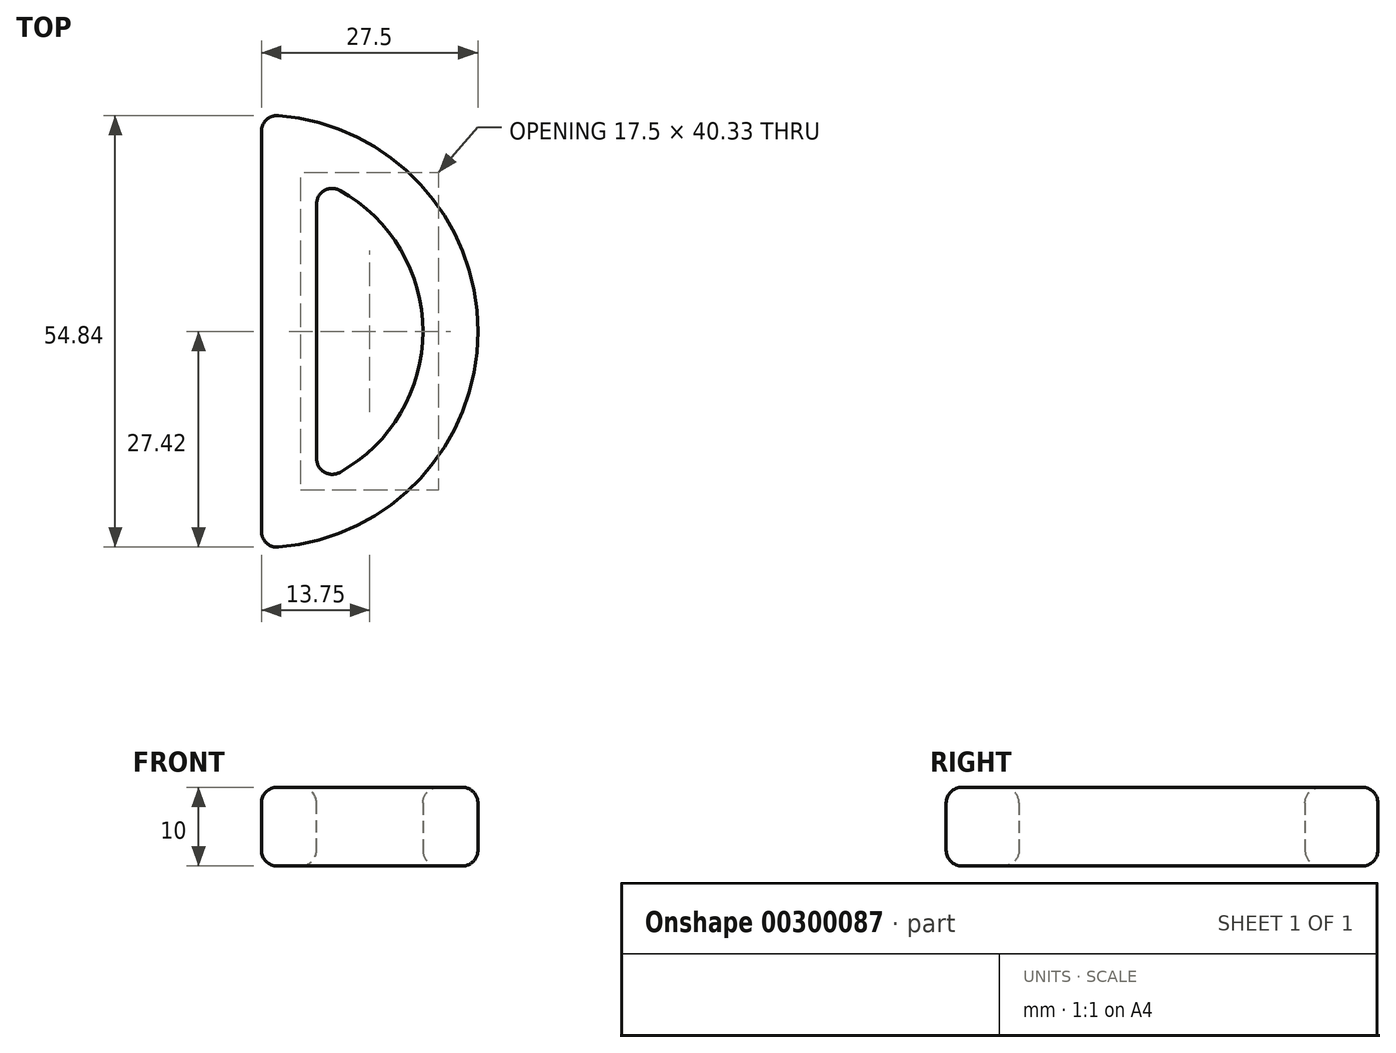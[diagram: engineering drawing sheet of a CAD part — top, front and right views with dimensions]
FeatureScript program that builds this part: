
annotation { "Feature Type Name" : "Feature", "Feature Type Description" : "" }
export const myFeature = defineFeature(function(context is Context, id is Id, definition is map)
    precondition{}
    {
        {
            var Q0;
            Q0=qCreatedBy(makeId("Top.planeOp"),FACE);
            var sketch = newSketch(context, id + "F0", { "sketchPlane" : qUnion([Q0])});
            skLineSegment(sketch, "E0", {"start": v(0, 0) * mm, "end": v(0, 55) * mm});
            skArc(sketch, "E1", {"start": v(0, 55) * mm, "mid": v(27.5, 27.5) * mm, "end": v(0, 0) * mm});
            skArc(sketch, "E2.0", {"start": v(0, 48) * mm, "mid": v(20.5, 27.5) * mm, "end": v(0, 7) * mm});
            skLineSegment(sketch, "E3", {"start": v(0, 27.5) * mm, "end": v(7, 27.5) * mm});
            skLineSegment(sketch, "E4", {"start": v(7, 27.5) * mm, "end": v(7, 46.77) * mm});
            skLineSegment(sketch, "E5", {"start": v(7, 27.5) * mm, "end": v(7, 8.23) * mm});
            skSolve(sketch);
        }
        {
            var Q0;
            Q0 = qSketchRegion(id + "F0", true);
            extrude(context, id + "F1", {"entities" : qUnion([Q0]), "depth" : 10 * mm});
        }
        {
            var Q0;
            Q0=makeQuery(id+"F1.opExtrude","SWEPT_FACE",FACE,{"disambiguationData":[OSD([sQuery(id+"F0.wireOp",EDGE,"E1")])]});
            var Q1;
            Q1=makeQuery(id+"F1.opExtrude","CAP_EDGE",EDGE,{"disambiguationData":[OSD([sQuery(id+"F0.wireOp",EDGE,"E2.0")])],"isStart":false});
            var Q2;
            Q2=makeQuery(id+"F1.opExtrude","CAP_EDGE",EDGE,{"disambiguationData":[OSD([sQuery(id+"F0.wireOp",EDGE,"E4"),sQuery(id+"F0.wireOp",EDGE,"E5")])],"isStart":false});
            var Q3;
            Q3=makeQuery(id+"F1.opExtrude","CAP_EDGE",EDGE,{"disambiguationData":[OSD([sQuery(id+"F0.wireOp",EDGE,"E0")])],"isStart":false});
            var Q4;
            Q4=makeQuery(id+"F1.opExtrude","CAP_EDGE",EDGE,{"disambiguationData":[OSD([sQuery(id+"F0.wireOp",EDGE,"E1")])],"isStart":false});
            var Q5;
            {var subQ0=sQuery(id+"F0.wireOp",EDGE,"E1");var subQ1=sQuery(id+"F0.wireOp",EDGE,"E0");Q5=makeQuery(id+"F1.opExtrude","SWEPT_EDGE",EDGE,{"disambiguationData":[OSD([subQ1,subQ0]),TDD([makeQuery(id+"F0.imprint","INTERSECT",VERTEX,{"disambiguationData":[OD(0.0)],"derivedFrom":[subQ1,subQ0]})])]});}
            var Q6;
            Q6=makeQuery(id+"F1.opExtrude","CAP_EDGE",EDGE,{"disambiguationData":[OSD([sQuery(id+"F0.wireOp",EDGE,"E2.0")])],"isStart":true});
            var Q7;
            Q7=makeQuery(id+"F1.opExtrude","CAP_EDGE",EDGE,{"disambiguationData":[OSD([sQuery(id+"F0.wireOp",EDGE,"E0")])],"isStart":true});
            var Q8;
            Q8=makeQuery(id+"F1.opExtrude","CAP_EDGE",EDGE,{"disambiguationData":[OSD([sQuery(id+"F0.wireOp",EDGE,"E4"),sQuery(id+"F0.wireOp",EDGE,"E5")])],"isStart":true});
            var Q9;
            Q9=makeQuery(id+"F1.opExtrude","SWEPT_EDGE",EDGE,{"disambiguationData":[OSD([sQuery(id+"F0.wireOp",EDGE,"E2.0"),sQuery(id+"F0.wireOp",EDGE,"E5")])]});
            var Q10;
            Q10=makeQuery(id+"F1.opExtrude","SWEPT_FACE",FACE,{"disambiguationData":[OSD([sQuery(id+"F0.wireOp",EDGE,"E4"),sQuery(id+"F0.wireOp",EDGE,"E5")])]});
            fillet(context, id + "F2", {"entities" : qUnion([Q0, Q1, Q2, Q3, Q4, Q5, Q6, Q7, Q8, Q9, Q10]), "radius" : 2 * mm, "tangentPropagation" : true, "allowEdgeOverflow" : false});
        }
    });
